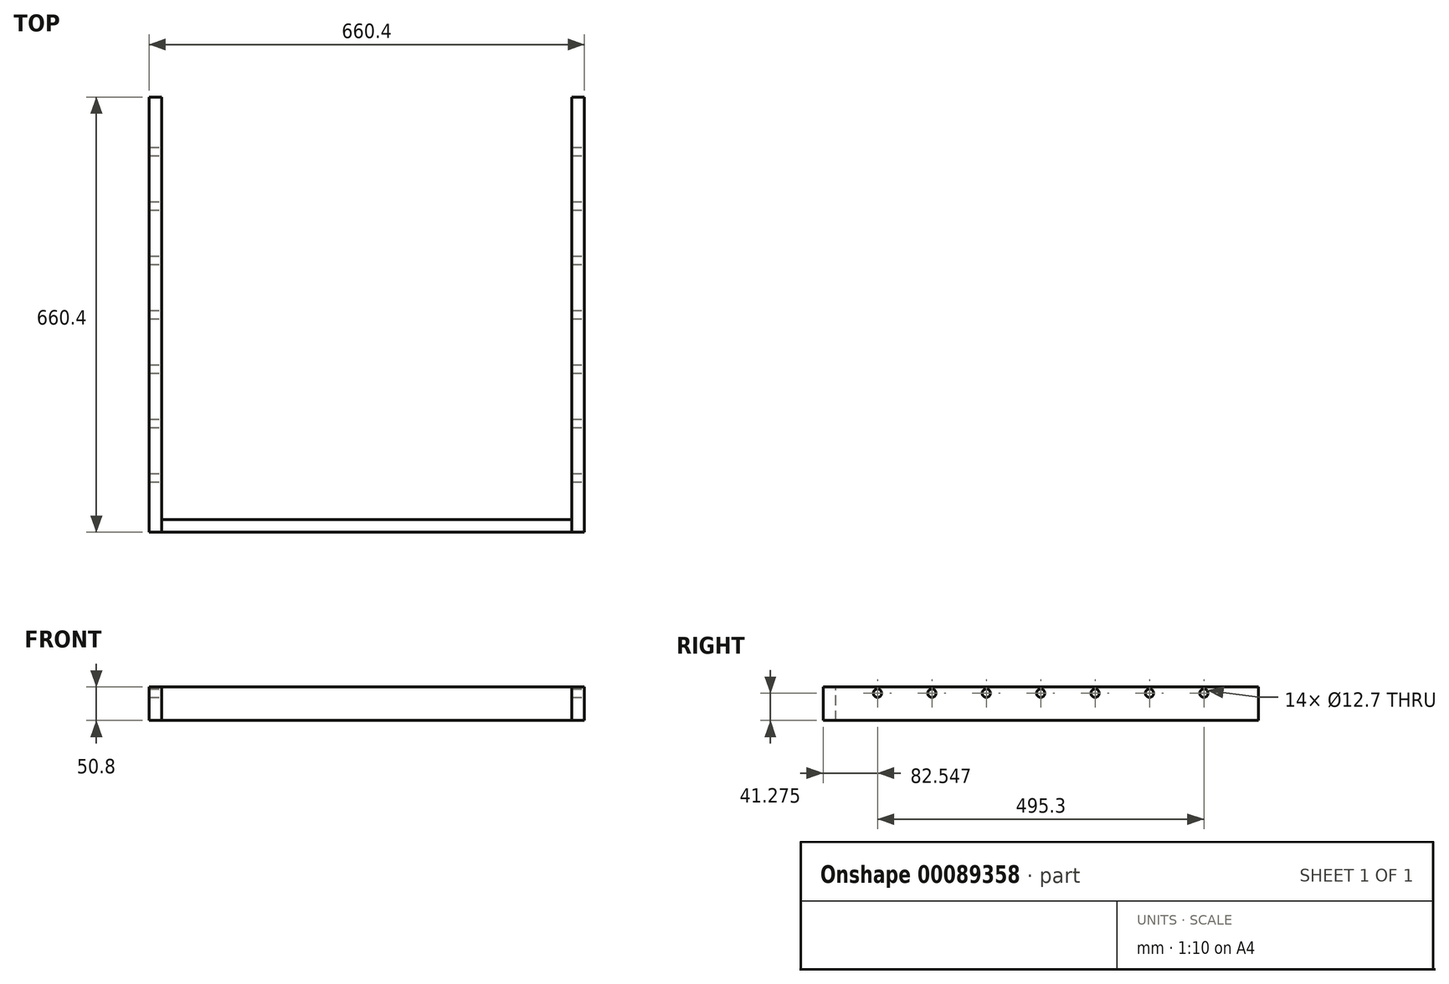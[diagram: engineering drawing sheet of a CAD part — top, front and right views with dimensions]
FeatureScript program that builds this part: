
annotation { "Feature Type Name" : "Feature", "Feature Type Description" : "" }
export const myFeature = defineFeature(function(context is Context, id is Id, definition is map)
    precondition{}
    {
        {
            var Q0;
            Q0=qCreatedBy(makeId("Top.planeOp"),FACE);
            var sketch = newSketch(context, id + "F0", { "sketchPlane" : qUnion([Q0])});
            skLineSegment(sketch, "E0.bottom", {"start": v(-58.09, -64.83) * mm, "end": v(602.31, -64.83) * mm});
            skLineSegment(sketch, "E0.top", {"start": v(-58.09, 595.57) * mm, "end": v(602.31, 595.57) * mm});
            skLineSegment(sketch, "E0.left", {"start": v(-58.09, -64.83) * mm, "end": v(-58.09, 595.57) * mm});
            skLineSegment(sketch, "E0.right", {"start": v(602.31, -64.83) * mm, "end": v(602.31, 595.57) * mm});
            skSolve(sketch);
        }
        {
            var Q0;
            Q0 = qSketchRegion(id + "F0", true);
            extrude(context, id + "F1", {"entities" : qUnion([Q0]), "depth" : 19.05 * mm});
        }
        {
            var Q0;
            Q0=makeQuery(id+"F1.opExtrude","SWEPT_FACE",FACE,{"disambiguationData":[OSD([sQuery(id+"F0.wireOp",EDGE,"E0.right")])]});
            var sketch = newSketch(context, id + "F2", { "sketchPlane" : qUnion([Q0])});
            skLineSegment(sketch, "E1.0", {"start": v(265.37, 19.05) * mm, "end": v(265.37, 0) * mm});
            skCircle(sketch, "E2", {"center": v(265.37, 9.53) * mm, "radius": 6.35 * mm});
            skLineSegment(sketch, "E3.0", {"start": v(100.27, 19.05) * mm, "end": v(100.27, 0) * mm});
            skLineSegment(sketch, "E4.0", {"start": v(430.47, 19.05) * mm, "end": v(430.47, 0) * mm});
            skCircle(sketch, "E5", {"center": v(100.27, 9.53) * mm, "radius": 6.35 * mm});
            skCircle(sketch, "E6", {"center": v(430.47, 9.53) * mm, "radius": 6.35 * mm});
            skLineSegment(sketch, "E7.0", {"start": v(182.82, 19.05) * mm, "end": v(182.82, 0) * mm});
            skCircle(sketch, "E8", {"center": v(182.82, 9.52) * mm, "radius": 6.35 * mm});
            skLineSegment(sketch, "E9.0", {"start": v(347.92, 19.05) * mm, "end": v(347.92, 0) * mm});
            skCircle(sketch, "E10", {"center": v(347.92, 9.53) * mm, "radius": 6.35 * mm});
            skLineSegment(sketch, "E11.0", {"start": v(17.72, 19.05) * mm, "end": v(17.72, 0) * mm});
            skLineSegment(sketch, "E12.0", {"start": v(513.02, 19.05) * mm, "end": v(513.02, 0) * mm});
            skCircle(sketch, "E13", {"center": v(17.72, 9.53) * mm, "radius": 6.35 * mm});
            skCircle(sketch, "E14", {"center": v(513.02, 9.52) * mm, "radius": 6.35 * mm});
            skSolve(sketch);
        }
        {
            var Q0;
            {var subQ0=sQuery(id+"F2.wireOp",EDGE,"E2");var subQ1=sQuery(id+"F2.wireOp",EDGE,"E1.0");var subQ2=makeQuery(id+"F2.imprint","INTERSECT",VERTEX,{"disambiguationData":[OD(0.0)],"derivedFrom":[subQ1,subQ0]});Q0=makeQuery(id+"F2.imprint","IMPRINT",FACE,{"disambiguationData":[TD([[makeQuery(id+"F2.imprint","IMPRINT",EDGE,{"disambiguationData":[TD([[subQ2,-1.0]])],"derivedFrom":subQ1}),-1.0]])]});}
            var Q1;
            {var subQ0=sQuery(id+"F2.wireOp",EDGE,"E5");var subQ1=sQuery(id+"F2.wireOp",EDGE,"E3.0");var subQ2=makeQuery(id+"F2.imprint","INTERSECT",VERTEX,{"disambiguationData":[OD(0.0)],"derivedFrom":[subQ1,subQ0]});Q1=makeQuery(id+"F2.imprint","IMPRINT",FACE,{"disambiguationData":[TD([[makeQuery(id+"F2.imprint","IMPRINT",EDGE,{"disambiguationData":[TD([[subQ2,-1.0]])],"derivedFrom":subQ1}),-1.0]])]});}
            var Q2;
            {var subQ0=sQuery(id+"F2.wireOp",EDGE,"E6");var subQ1=sQuery(id+"F2.wireOp",EDGE,"E4.0");var subQ2=makeQuery(id+"F2.imprint","INTERSECT",VERTEX,{"disambiguationData":[OD(0.0)],"derivedFrom":[subQ1,subQ0]});Q2=makeQuery(id+"F2.imprint","IMPRINT",FACE,{"disambiguationData":[TD([[makeQuery(id+"F2.imprint","IMPRINT",EDGE,{"disambiguationData":[TD([[subQ2,-1.0]])],"derivedFrom":subQ1}),1.0]])]});}
            var Q3;
            {var subQ0=sQuery(id+"F2.wireOp",EDGE,"E8");var subQ1=sQuery(id+"F2.wireOp",EDGE,"E7.0");var subQ2=makeQuery(id+"F2.imprint","INTERSECT",VERTEX,{"disambiguationData":[OD(0.0)],"derivedFrom":[subQ1,subQ0]});Q3=makeQuery(id+"F2.imprint","IMPRINT",FACE,{"disambiguationData":[TD([[makeQuery(id+"F2.imprint","IMPRINT",EDGE,{"disambiguationData":[TD([[subQ2,-1.0]])],"derivedFrom":subQ1}),-1.0]])]});}
            var Q4;
            {var subQ0=sQuery(id+"F2.wireOp",EDGE,"E10");var subQ1=sQuery(id+"F2.wireOp",EDGE,"E9.0");var subQ2=makeQuery(id+"F2.imprint","INTERSECT",VERTEX,{"disambiguationData":[OD(0.0)],"derivedFrom":[subQ1,subQ0]});Q4=makeQuery(id+"F2.imprint","IMPRINT",FACE,{"disambiguationData":[TD([[makeQuery(id+"F2.imprint","IMPRINT",EDGE,{"disambiguationData":[TD([[subQ2,-1.0]])],"derivedFrom":subQ1}),-1.0]])]});}
            var Q5;
            {var subQ0=sQuery(id+"F2.wireOp",EDGE,"E13");var subQ1=sQuery(id+"F2.wireOp",EDGE,"E11.0");var subQ2=makeQuery(id+"F2.imprint","INTERSECT",VERTEX,{"disambiguationData":[OD(0.0)],"derivedFrom":[subQ1,subQ0]});Q5=makeQuery(id+"F2.imprint","IMPRINT",FACE,{"disambiguationData":[TD([[makeQuery(id+"F2.imprint","IMPRINT",EDGE,{"disambiguationData":[TD([[subQ2,-1.0]])],"derivedFrom":subQ1}),-1.0]])]});}
            var Q6;
            {var subQ0=sQuery(id+"F2.wireOp",EDGE,"E13");var subQ1=sQuery(id+"F2.wireOp",EDGE,"E11.0");var subQ2=makeQuery(id+"F2.imprint","INTERSECT",VERTEX,{"disambiguationData":[OD(0.0)],"derivedFrom":[subQ1,subQ0]});Q6=makeQuery(id+"F2.imprint","IMPRINT",FACE,{"disambiguationData":[TD([[makeQuery(id+"F2.imprint","IMPRINT",EDGE,{"disambiguationData":[TD([[subQ2,-1.0]])],"derivedFrom":subQ1}),1.0]])]});}
            var Q7;
            {var subQ0=sQuery(id+"F2.wireOp",EDGE,"E14");var subQ1=sQuery(id+"F2.wireOp",EDGE,"E12.0");var subQ2=makeQuery(id+"F2.imprint","INTERSECT",VERTEX,{"disambiguationData":[OD(0.0)],"derivedFrom":[subQ1,subQ0]});Q7=makeQuery(id+"F2.imprint","IMPRINT",FACE,{"disambiguationData":[TD([[makeQuery(id+"F2.imprint","IMPRINT",EDGE,{"disambiguationData":[TD([[subQ2,-1.0]])],"derivedFrom":subQ1}),-1.0]])]});}
            var Q8;
            {var subQ0=sQuery(id+"F2.wireOp",EDGE,"E14");var subQ1=sQuery(id+"F2.wireOp",EDGE,"E12.0");var subQ2=makeQuery(id+"F2.imprint","INTERSECT",VERTEX,{"disambiguationData":[OD(0.0)],"derivedFrom":[subQ1,subQ0]});Q8=makeQuery(id+"F2.imprint","IMPRINT",FACE,{"disambiguationData":[TD([[makeQuery(id+"F2.imprint","IMPRINT",EDGE,{"disambiguationData":[TD([[subQ2,-1.0]])],"derivedFrom":subQ1}),1.0]])]});}
            var Q9;
            {var subQ0=sQuery(id+"F2.wireOp",EDGE,"E6");var subQ1=sQuery(id+"F2.wireOp",EDGE,"E4.0");var subQ2=makeQuery(id+"F2.imprint","INTERSECT",VERTEX,{"disambiguationData":[OD(0.0)],"derivedFrom":[subQ1,subQ0]});Q9=makeQuery(id+"F2.imprint","IMPRINT",FACE,{"disambiguationData":[TD([[makeQuery(id+"F2.imprint","IMPRINT",EDGE,{"disambiguationData":[TD([[subQ2,-1.0]])],"derivedFrom":subQ1}),-1.0]])]});}
            var Q10;
            {var subQ0=sQuery(id+"F2.wireOp",EDGE,"E10");var subQ1=sQuery(id+"F2.wireOp",EDGE,"E9.0");var subQ2=makeQuery(id+"F2.imprint","INTERSECT",VERTEX,{"disambiguationData":[OD(0.0)],"derivedFrom":[subQ1,subQ0]});Q10=makeQuery(id+"F2.imprint","IMPRINT",FACE,{"disambiguationData":[TD([[makeQuery(id+"F2.imprint","IMPRINT",EDGE,{"disambiguationData":[TD([[subQ2,-1.0]])],"derivedFrom":subQ1}),1.0]])]});}
            var Q11;
            {var subQ0=sQuery(id+"F2.wireOp",EDGE,"E2");var subQ1=sQuery(id+"F2.wireOp",EDGE,"E1.0");var subQ2=makeQuery(id+"F2.imprint","INTERSECT",VERTEX,{"disambiguationData":[OD(0.0)],"derivedFrom":[subQ1,subQ0]});Q11=makeQuery(id+"F2.imprint","IMPRINT",FACE,{"disambiguationData":[TD([[makeQuery(id+"F2.imprint","IMPRINT",EDGE,{"disambiguationData":[TD([[subQ2,-1.0]])],"derivedFrom":subQ1}),1.0]])]});}
            var Q12;
            {var subQ0=sQuery(id+"F2.wireOp",EDGE,"E5");var subQ1=sQuery(id+"F2.wireOp",EDGE,"E3.0");var subQ2=makeQuery(id+"F2.imprint","INTERSECT",VERTEX,{"disambiguationData":[OD(0.0)],"derivedFrom":[subQ1,subQ0]});Q12=makeQuery(id+"F2.imprint","IMPRINT",FACE,{"disambiguationData":[TD([[makeQuery(id+"F2.imprint","IMPRINT",EDGE,{"disambiguationData":[TD([[subQ2,-1.0]])],"derivedFrom":subQ1}),1.0]])]});}
            var Q13;
            {var subQ0=sQuery(id+"F2.wireOp",EDGE,"E8");var subQ1=sQuery(id+"F2.wireOp",EDGE,"E7.0");var subQ2=makeQuery(id+"F2.imprint","INTERSECT",VERTEX,{"disambiguationData":[OD(0.0)],"derivedFrom":[subQ1,subQ0]});Q13=makeQuery(id+"F2.imprint","IMPRINT",FACE,{"disambiguationData":[TD([[makeQuery(id+"F2.imprint","IMPRINT",EDGE,{"disambiguationData":[TD([[subQ2,-1.0]])],"derivedFrom":subQ1}),1.0]])]});}
            extrude(context, id + "F3", {"entities" : qUnion([Q0, Q1, Q2, Q3, Q4, Q5, Q6, Q7, Q8, Q9, Q10, Q11, Q12, Q13]), "operationType" : NewBodyOperationType.REMOVE, "endBound" : BoundingType.THROUGH_ALL, "oppositeDirection" : true, "depth" : 6.35 * mm});
        }
        {
            var Q0;
            Q0=makeQuery(id+"F1.opExtrude","CAP_FACE",FACE,{"disambiguationData":[OSD([sQuery(id+"F0.wireOp",EDGE,"E0.bottom"),sQuery(id+"F0.wireOp",EDGE,"E0.top"),sQuery(id+"F0.wireOp",EDGE,"E0.left"),sQuery(id+"F0.wireOp",EDGE,"E0.right")])],"isStart":false});
            var sketch = newSketch(context, id + "F4", { "sketchPlane" : qUnion([Q0])});
            skLineSegment(sketch, "E15.0", {"start": v(-39.04, 576.52) * mm, "end": v(583.26, 576.52) * mm});
            skLineSegment(sketch, "E15.1", {"start": v(-39.04, -45.78) * mm, "end": v(-39.04, 576.52) * mm});
            skLineSegment(sketch, "E15.2", {"start": v(-39.04, -45.78) * mm, "end": v(583.26, -45.78) * mm});
            skLineSegment(sketch, "E15.3", {"start": v(583.26, -45.78) * mm, "end": v(583.26, 576.52) * mm});
            skSolve(sketch);
        }
        {
            var Q0;
            Q0=makeQuery(id+"F4.imprint","IMPRINT",FACE,{"disambiguationData":[TD([[makeQuery(id+"F4.imprint","IMPRINT",EDGE,{"derivedFrom":sQuery(id+"F4.wireOp",EDGE,"E15.0")}),-1.0]])]});
            extrude(context, id + "F5", {"entities" : qUnion([Q0]), "operationType" : NewBodyOperationType.REMOVE, "endBound" : BoundingType.THROUGH_ALL, "oppositeDirection" : true, "depth" : 25.4 * mm});
        }
        {
            var Q0;
            Q0 = qSketchRegion(id + "F2", true);
            extrude(context, id + "F6", {"entities" : qUnion([Q0]), "oppositeDirection" : true, "depth" : 660.4 * mm});
        }
        {
            var Q0;
            Q0=makeQuery(id+"F1.opExtrude","CAP_FACE",FACE,{"disambiguationData":[OSD([sQuery(id+"F0.wireOp",EDGE,"E0.bottom"),sQuery(id+"F0.wireOp",EDGE,"E0.top"),sQuery(id+"F0.wireOp",EDGE,"E0.left"),sQuery(id+"F0.wireOp",EDGE,"E0.right")])],"isStart":true});
            extrude(context, id + "F7", {"entities" : qUnion([Q0]), "operationType" : NewBodyOperationType.ADD, "depth" : 31.75 * mm});
        }
        {
            var Q0;
            {var subQ0=sQuery(id+"F0.wireOp",EDGE,"E0.bottom");Q0=makeQuery(id+"F7.boolean.opBoolean","MERGE",FACE,{"derivedFrom":[makeQuery(id+"F1.opExtrude","SWEPT_FACE",FACE,{"disambiguationData":[OSD([subQ0])]}),makeQuery(id+"F7.opExtrude","SWEPT_FACE",FACE,{"disambiguationData":[OSD([subQ0])]})]});}
            var sketch = newSketch(context, id + "F8", { "sketchPlane" : qUnion([Q0])});
            skLineSegment(sketch, "E16", {"start": v(-58.09, -6.35) * mm, "end": v(-39.04, -6.35) * mm, "construction": true});
            skLineSegment(sketch, "E17", {"start": v(602.31, -6.35) * mm, "end": v(583.26, -6.35) * mm, "construction": true});
            skLineSegment(sketch, "E18", {"start": v(-39.04, -31.75) * mm, "end": v(-39.04, 19.05) * mm});
            skLineSegment(sketch, "E19", {"start": v(583.26, -31.75) * mm, "end": v(583.26, 19.05) * mm});
            skLineSegment(sketch, "E20", {"start": v(583.26, 19.05) * mm, "end": v(-39.04, 19.05) * mm});
            skLineSegment(sketch, "E21", {"start": v(-39.04, -31.75) * mm, "end": v(583.26, -31.75) * mm});
            skSolve(sketch);
        }
        {
            var Q0;
            Q0=makeQuery(id+"F8.imprint","IMPRINT",FACE,{"disambiguationData":[TD([[makeQuery(id+"F8.imprint","IMPRINT",EDGE,{"derivedFrom":sQuery(id+"F8.wireOp",EDGE,"E18")}),-1.0]])]});
            extrude(context, id + "F9", {"entities" : qUnion([Q0]), "operationType" : NewBodyOperationType.REMOVE, "endBound" : BoundingType.THROUGH_ALL, "oppositeDirection" : true, "depth" : 25.4 * mm});
        }
        {
            var Q0;
            Q0 = qSketchRegion(id + "F8", true);
            extrude(context, id + "F10", {"entities" : qUnion([Q0]), "oppositeDirection" : true, "depth" : 19.05 * mm});
        }
    });
